# Revit family: WCPan-WallHung-54cm-Vitra_SentoSeries_4448
name_source: partatom
category: Plumbing Fixtures
revit_build: Autodesk Revit 2017 (Build: 20160225_1515(x64)
units: mm (PartAtom-declared; Revit-internal decimal feet)

## family parameters
Cut with Voids When Loaded = No
Host = Face
OmniClass Number = 23.45.05.21.11
OmniClass Title = Water Closets
Part Type = Normal
Room Calculation Point = No
Round Connector Dimension = Use Diameter
Shared = Yes

## types (6) — shared parameters
BIMobject category = Sanitary - Toilets
Brand = VitrA
CW Connection = Yes
Color = White
Default Elevation = 410 mm  [stored 1.34514 ft]
Design country = Turkey
HW Connection = No
IFC Classification = Sanitary Terminal
Main Material = Ceramic
Manufacturer = VitrA
Manufacturer name = VitrA
Masterformat 2014 Code = 22 45 26
Masterformat 2014 Description = Sanitary Facilities
Mounting type = Wall-Hung
NBS Referans Code = 35-65-90
NBS Referans Description = Toilet Systems
Nominal Depth (mm) = 540 mm  [stored 1.77165 ft]
Nominal Height (mm) = 340 mm  [stored 1.11549 ft]
Nominal Width (mm) = 365 mm  [stored 1.19751 ft]
OmniClass Code = 23-31 19 00
OmniClass Description = Toilets
Primary Material = White
Product certification = https://www.vitraglobal.com
Product family = Sento
Product group = Wall Mounted WC
UNSPSC Code = 301815
UNSPSC Description = Sanitary Ware
URL = https://www.vitraglobal.com
Uniclass 1.4 Code = L7216
Uniclass 1.4 Description = Toilets
Uniclass 2.0 Code = SS-35-65-90
Uniclass 2.0 Description = Toilet Systems
Uniclass 2015 Code = Pr_40_20_93
Uniclass 2015 Name = Urinal and WC fittings
Uniformat II Code = D2010
Uniformat II Description = Sanitary Facilities
Vent Connection = No
Warranty Period (Year) = 10 Years
Waste Connection = Yes
Weight Net (kg) = 28.7
Youtube = https://www.youtube.com

## per-type parameters (varying)
| type | Article No. (default) | Description | Model | Product SKU | Product data url | Product url | Secondary Material | Technical description | With Bidet Function | With Stop Valve | With Thermostatic Stop Valve |
| WCPan-WallHung-54cm_Vitra_Sento_4448B003-0075 | 4448B003-7211 | VitrA Sento With Bidet Function - With Thermostatic Stop Valve - Wall-Hung - 54cm - Wc Pan | 4448B003-7211 | 4448B003-7211 | https://www.bimobject.com | https://www.vitraglobal.com | <By Category> | https://www.vitraglobal.com | Yes | Yes | Yes |
| WCPan-WallHung-54cm-VitraClean_Vitra_Sento_4448B403-0075 | 4448B403-0075 | VitrA Sento (Vitra Clean) Without Bidet Function - Wall-Hung - 54cm - Wc Pan | 4448B403-0075 | 4448B403-0075 | https://www.vitra-bad.de |  | <By Category> | https://cdn.vitra.com.tr | No | No | No |
| WCPan-WallHung-54cm-WithBidetFunction_Vitra_Sento_4448B003-0559 | 4448B003-0559 | VitrA Sento With Bidet Function - Wall-Hung - 54cm - Wc Pan | 4448B003-0559 | 4448B003-0559 | https://www.vitra-bad.de |  | <By Category> | https://www.vitra-bad.de | Yes | No | Yes |
| WCPan-WallHung-54cm-VitraClean-WithBidetFunction_Vitra_Sento_4448B403-0559 | 4448B403-0559 | VitrA Sento (Vitra Clean) With Bidet Function - Wall-Hung - 54cm - Wc Pan | 4448B403-0559 | 4448B403-0559 | https://www.vitra-bad.de |  | <By Category> | https://www.vitra-bad.de | Yes | No | No |
| WCPan-WallHung-54cm-WithBidetFunction-WithStopValve_Vitra_Sento_4448B003-1684 | 4448B003-1684 | VitrA Sento With Bidet Function - With Stop Valve - Wall-Hung - 54cm - Wc Pan | 4448B003-1684 | 4448B003-1684 | https://www.vitraglobal.com |  | Chrome | https://www.vitraglobal.com | Yes | Yes | No |
| WCPan-WallHung-54cm-WithBidetFunction-WithThermostaticStopValve_Vitra_Sento_4448B003-7211 | 4448B003-7211 | VitrA Sento With Bidet Function - With Thermostatic Stop Valve - Wall-Hung - 54cm - Wc Pan | 4448B003-7211 | 4448B003-7211 | https://www.vitraglobal.com |  | Chrome | https://www.vitraglobal.com | Yes | No | Yes |

note: [stored X ft] marks values corroborated as IEEE doubles in the binary element streams (Revit-internal decimal feet)

## geometry (parser evidence)
native form markers: Sweep x2
no freeform markers — native parametric forms only
